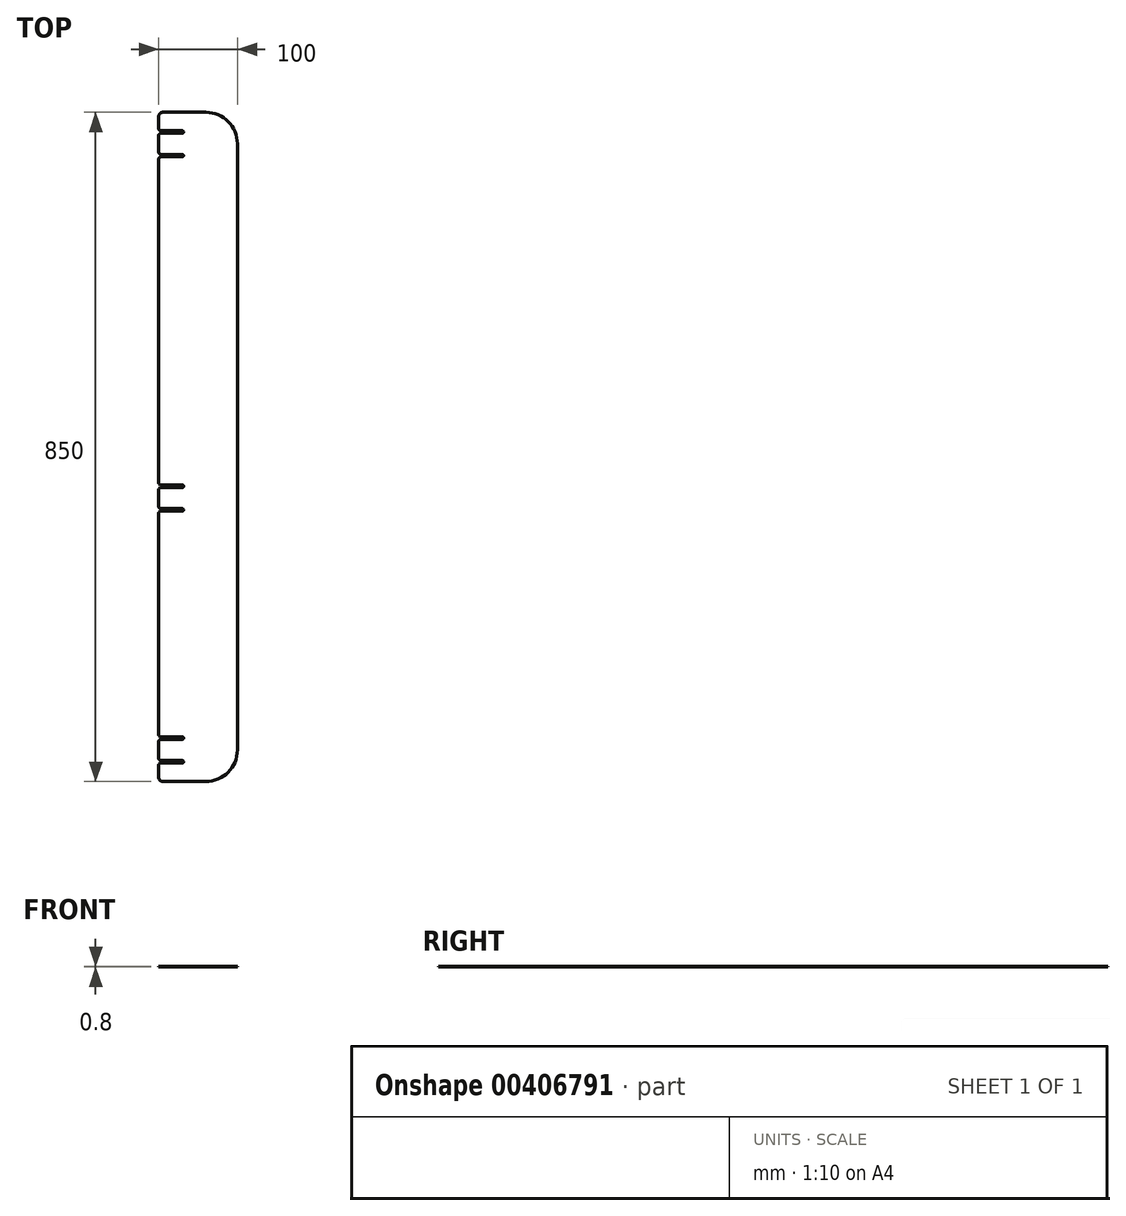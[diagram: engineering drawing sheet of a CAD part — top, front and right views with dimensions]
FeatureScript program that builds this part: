
annotation { "Feature Type Name" : "Feature", "Feature Type Description" : "" }
export const myFeature = defineFeature(function(context is Context, id is Id, definition is map)
    precondition{}
    {
        {
            var Q0;
            Q0=qCreatedBy(makeId("Top.planeOp"),FACE);
            var sketch = newSketch(context, id + "F0", { "sketchPlane" : qUnion([Q0])});
            skLineSegment(sketch, "E0.bottom", {"start": v(-95, 825) * mm, "end": v(-40, 825) * mm});
            skLineSegment(sketch, "E0.top", {"start": v(-95, -25) * mm, "end": v(-40, -25) * mm});
            skLineSegment(sketch, "E0.left", {"start": v(-100, 820) * mm, "end": v(-100, -20) * mm});
            skLineSegment(sketch, "E0.right", {"start": v(0, 785) * mm, "end": v(0, 15) * mm});
            skCircle(sketch, "E1", {"center": v(-70, 800) * mm, "radius": 1.5 * mm});
            skCircle(sketch, "E2", {"center": v(-70, 770) * mm, "radius": 1.5 * mm});
            skCircle(sketch, "E3", {"center": v(-70, 350) * mm, "radius": 1.5 * mm});
            skCircle(sketch, "E4", {"center": v(-70, 320) * mm, "radius": 1.5 * mm});
            skCircle(sketch, "E5", {"center": v(-70, 30) * mm, "radius": 1.5 * mm});
            skCircle(sketch, "E6", {"center": v(-70, 0) * mm, "radius": 1.5 * mm});
            skLineSegment(sketch, "E7", {"start": v(-70, 825) * mm, "end": v(-70, -25) * mm, "construction": true});
            skLineSegment(sketch, "E8.bottom", {"start": v(141.58, 765) * mm, "end": v(-337.65, 765) * mm, "construction": true});
            skLineSegment(sketch, "E8.top", {"start": v(141.58, 375) * mm, "end": v(-337.65, 375) * mm, "construction": true});
            skLineSegment(sketch, "E8.left", {"start": v(141.58, 765) * mm, "end": v(141.58, 375) * mm, "construction": true});
            skLineSegment(sketch, "E8.right", {"start": v(-337.65, 765) * mm, "end": v(-337.65, 375) * mm, "construction": true});
            skPoint(sketch, "E9.visualSharp", {"position": v(0, -25) * mm});
            skArc(sketch, "E9.filletArc", {"start": v(-40, -25) * mm, "mid": v(-11.72, -13.28) * mm, "end": v(0, 15) * mm});
            skPoint(sketch, "E10.visualSharp", {"position": v(0, 825) * mm});
            skArc(sketch, "E10.filletArc", {"start": v(0, 785) * mm, "mid": v(-11.72, 813.28) * mm, "end": v(-40, 825) * mm});
            skPoint(sketch, "E11.visualSharp", {"position": v(-100, -25) * mm});
            skArc(sketch, "E11.filletArc", {"start": v(-100, -20) * mm, "mid": v(-98.54, -23.54) * mm, "end": v(-95, -25) * mm});
            skPoint(sketch, "E12.visualSharp", {"position": v(-100, 825) * mm});
            skArc(sketch, "E12.filletArc", {"start": v(-95, 825) * mm, "mid": v(-98.54, 823.54) * mm, "end": v(-100, 820) * mm});
            skLineSegment(sketch, "E13.bottom", {"start": v(-70, 771.5) * mm, "end": v(-100, 771.5) * mm});
            skLineSegment(sketch, "E13.top", {"start": v(-70, 768.5) * mm, "end": v(-100, 768.5) * mm});
            skLineSegment(sketch, "E13.left", {"start": v(-70, 771.5) * mm, "end": v(-70, 768.5) * mm});
            skLineSegment(sketch, "E13.right", {"start": v(-100, 771.5) * mm, "end": v(-100, 768.5) * mm});
            skLineSegment(sketch, "E14.bottom", {"start": v(-70, 801.5) * mm, "end": v(-100, 801.5) * mm});
            skLineSegment(sketch, "E14.top", {"start": v(-70, 798.5) * mm, "end": v(-100, 798.5) * mm});
            skLineSegment(sketch, "E14.left", {"start": v(-70, 801.5) * mm, "end": v(-70, 798.5) * mm});
            skLineSegment(sketch, "E14.right", {"start": v(-100, 801.5) * mm, "end": v(-100, 798.5) * mm});
            skLineSegment(sketch, "E15.bottom", {"start": v(-70, 351.5) * mm, "end": v(-100, 351.5) * mm});
            skLineSegment(sketch, "E15.top", {"start": v(-70, 348.5) * mm, "end": v(-100, 348.5) * mm});
            skLineSegment(sketch, "E15.left", {"start": v(-70, 351.5) * mm, "end": v(-70, 348.5) * mm});
            skLineSegment(sketch, "E15.right", {"start": v(-100, 351.5) * mm, "end": v(-100, 348.5) * mm});
            skLineSegment(sketch, "E16.bottom", {"start": v(-70, 321.5) * mm, "end": v(-100, 321.5) * mm});
            skLineSegment(sketch, "E16.top", {"start": v(-70, 318.5) * mm, "end": v(-100, 318.5) * mm});
            skLineSegment(sketch, "E16.left", {"start": v(-70, 321.5) * mm, "end": v(-70, 318.5) * mm});
            skLineSegment(sketch, "E16.right", {"start": v(-100, 321.5) * mm, "end": v(-100, 318.5) * mm});
            skLineSegment(sketch, "E17.bottom", {"start": v(-70, 31.5) * mm, "end": v(-100, 31.5) * mm});
            skLineSegment(sketch, "E17.top", {"start": v(-70, 28.5) * mm, "end": v(-100, 28.5) * mm});
            skLineSegment(sketch, "E17.left", {"start": v(-70, 31.5) * mm, "end": v(-70, 28.5) * mm});
            skLineSegment(sketch, "E17.right", {"start": v(-100, 31.5) * mm, "end": v(-100, 28.5) * mm});
            skLineSegment(sketch, "E18.bottom", {"start": v(-70, 1.5) * mm, "end": v(-100, 1.5) * mm});
            skLineSegment(sketch, "E18.top", {"start": v(-70, -1.5) * mm, "end": v(-100, -1.5) * mm});
            skLineSegment(sketch, "E18.left", {"start": v(-70, 1.5) * mm, "end": v(-70, -1.5) * mm});
            skLineSegment(sketch, "E18.right", {"start": v(-100, 1.5) * mm, "end": v(-100, -1.5) * mm});
            skSolve(sketch);
        }
        {
            var Q0;
            Q0=makeQuery(id+"F0.imprint","IMPRINT",FACE,{"disambiguationData":[TD([[makeQuery(id+"F0.imprint","IMPRINT",EDGE,{"derivedFrom":sQuery(id+"F0.wireOp",EDGE,"E0.bottom")}),-1.0]])]});
            extrude(context, id + "F1", {"entities" : qUnion([Q0]), "depth" : 0.8 * mm});
        }
        {
            var Q0;
            Q0=makeQuery(id+"F1.opExtrude","SWEPT_EDGE",EDGE,{"disambiguationData":[OSD([sQuery(id+"F0.wireOp",EDGE,"E0.left"),sQuery(id+"F0.wireOp",EDGE,"E14.bottom"),sQuery(id+"F0.wireOp",EDGE,"E14.right")])]});
            var Q1;
            Q1=makeQuery(id+"F1.opExtrude","SWEPT_EDGE",EDGE,{"disambiguationData":[OSD([sQuery(id+"F0.wireOp",EDGE,"E0.left"),sQuery(id+"F0.wireOp",EDGE,"E14.top"),sQuery(id+"F0.wireOp",EDGE,"E14.right")])]});
            var Q2;
            Q2=makeQuery(id+"F1.opExtrude","SWEPT_EDGE",EDGE,{"disambiguationData":[OSD([sQuery(id+"F0.wireOp",EDGE,"E0.left"),sQuery(id+"F0.wireOp",EDGE,"E13.bottom"),sQuery(id+"F0.wireOp",EDGE,"E13.right")])]});
            var Q3;
            Q3=makeQuery(id+"F1.opExtrude","SWEPT_EDGE",EDGE,{"disambiguationData":[OSD([sQuery(id+"F0.wireOp",EDGE,"E0.left"),sQuery(id+"F0.wireOp",EDGE,"E13.top"),sQuery(id+"F0.wireOp",EDGE,"E13.right")])]});
            var Q4;
            Q4=makeQuery(id+"F1.opExtrude","SWEPT_EDGE",EDGE,{"disambiguationData":[OSD([sQuery(id+"F0.wireOp",EDGE,"E0.left"),sQuery(id+"F0.wireOp",EDGE,"E15.bottom"),sQuery(id+"F0.wireOp",EDGE,"E15.right")])]});
            var Q5;
            Q5=makeQuery(id+"F1.opExtrude","SWEPT_EDGE",EDGE,{"disambiguationData":[OSD([sQuery(id+"F0.wireOp",EDGE,"E0.left"),sQuery(id+"F0.wireOp",EDGE,"E15.top"),sQuery(id+"F0.wireOp",EDGE,"E15.right")])]});
            var Q6;
            Q6=makeQuery(id+"F1.opExtrude","SWEPT_EDGE",EDGE,{"disambiguationData":[OSD([sQuery(id+"F0.wireOp",EDGE,"E0.left"),sQuery(id+"F0.wireOp",EDGE,"E16.bottom"),sQuery(id+"F0.wireOp",EDGE,"E16.right")])]});
            var Q7;
            Q7=makeQuery(id+"F1.opExtrude","SWEPT_EDGE",EDGE,{"disambiguationData":[OSD([sQuery(id+"F0.wireOp",EDGE,"E0.left"),sQuery(id+"F0.wireOp",EDGE,"E16.top"),sQuery(id+"F0.wireOp",EDGE,"E16.right")])]});
            var Q8;
            Q8=makeQuery(id+"F1.opExtrude","SWEPT_EDGE",EDGE,{"disambiguationData":[OSD([sQuery(id+"F0.wireOp",EDGE,"E0.left"),sQuery(id+"F0.wireOp",EDGE,"E17.bottom"),sQuery(id+"F0.wireOp",EDGE,"E17.right")])]});
            var Q9;
            Q9=makeQuery(id+"F1.opExtrude","SWEPT_EDGE",EDGE,{"disambiguationData":[OSD([sQuery(id+"F0.wireOp",EDGE,"E0.left"),sQuery(id+"F0.wireOp",EDGE,"E17.top"),sQuery(id+"F0.wireOp",EDGE,"E17.right")])]});
            var Q10;
            Q10=makeQuery(id+"F1.opExtrude","SWEPT_EDGE",EDGE,{"disambiguationData":[OSD([sQuery(id+"F0.wireOp",EDGE,"E0.left"),sQuery(id+"F0.wireOp",EDGE,"E18.bottom"),sQuery(id+"F0.wireOp",EDGE,"E18.right")])]});
            var Q11;
            Q11=makeQuery(id+"F1.opExtrude","SWEPT_EDGE",EDGE,{"disambiguationData":[OSD([sQuery(id+"F0.wireOp",EDGE,"E0.left"),sQuery(id+"F0.wireOp",EDGE,"E18.top"),sQuery(id+"F0.wireOp",EDGE,"E18.right")])]});
            fillet(context, id + "F2", {"entities" : qUnion([Q0, Q1, Q2, Q3, Q4, Q5, Q6, Q7, Q8, Q9, Q10, Q11]), "radius" : 3 * mm, "tangentPropagation" : true, "allowEdgeOverflow" : false});
        }
    });
